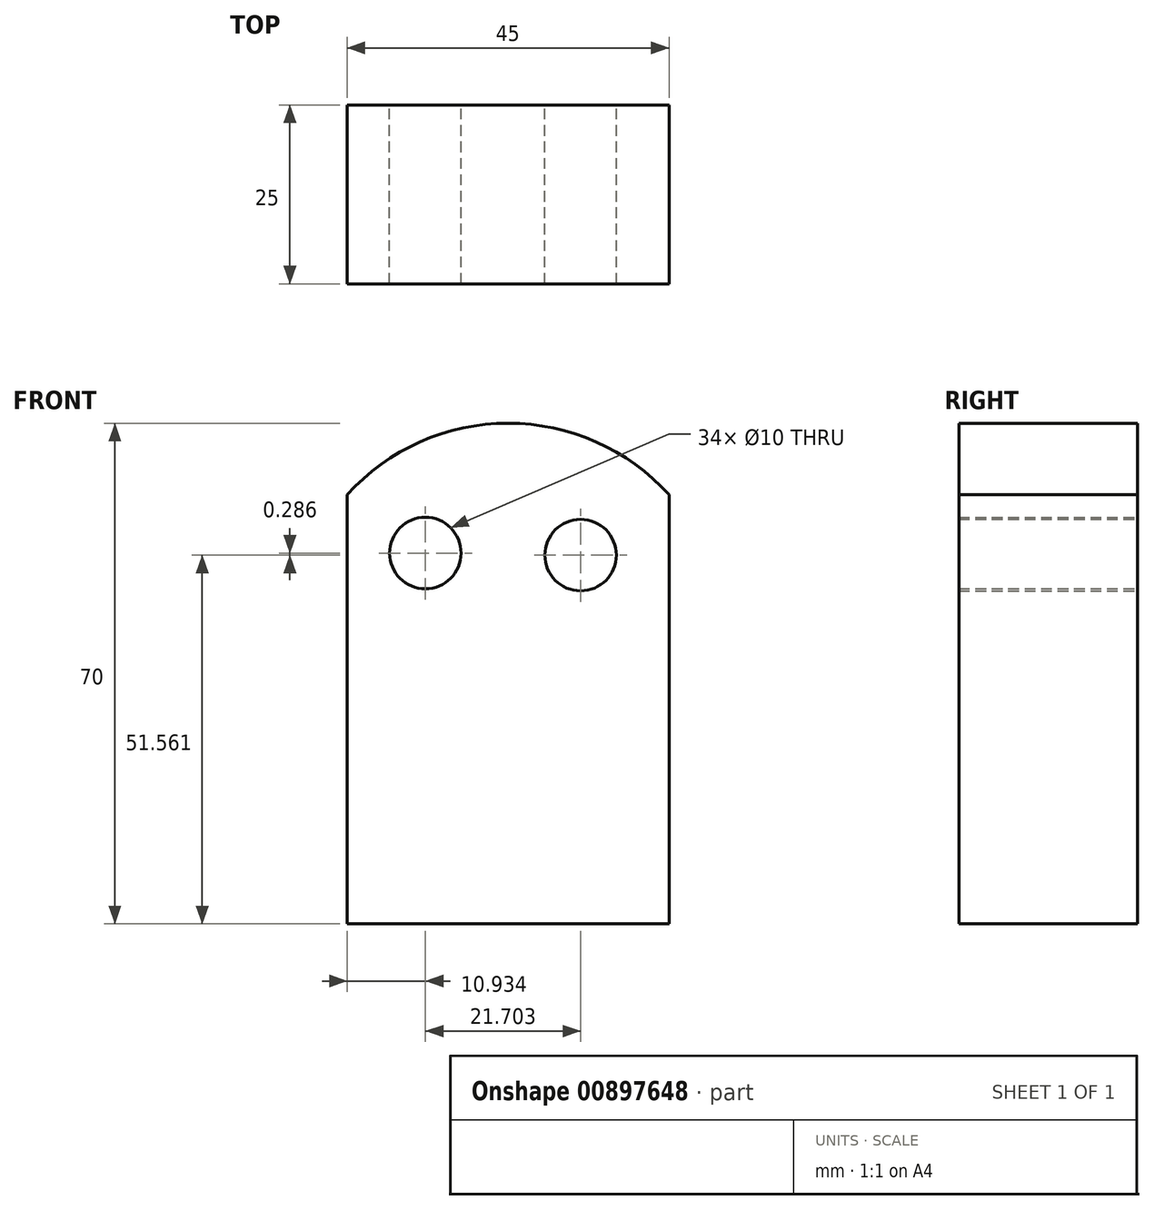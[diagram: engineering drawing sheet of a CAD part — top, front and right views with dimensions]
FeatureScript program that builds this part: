
annotation { "Feature Type Name" : "Feature", "Feature Type Description" : "" }
export const myFeature = defineFeature(function(context is Context, id is Id, definition is map)
    precondition{}
    {
        {
            var Q0;
            Q0=qCreatedBy(makeId("Front.planeOp"),FACE);
            var sketch = newSketch(context, id + "F0", { "sketchPlane" : qUnion([Q0])});
            skLineSegment(sketch, "E0.bottom", {"start": v(-22.5, 30) * mm, "end": v(22.5, 30) * mm});
            skLineSegment(sketch, "E0.top", {"start": v(-22.5, -30) * mm, "end": v(22.5, -30) * mm});
            skLineSegment(sketch, "E0.left", {"start": v(-22.5, 30) * mm, "end": v(-22.5, -30) * mm});
            skLineSegment(sketch, "E0.right", {"start": v(22.5, 30) * mm, "end": v(22.5, -30) * mm});
            skPoint(sketch, "E0.middle", {"position": v(0, 0) * mm});
            skArc(sketch, "E1", {"start": v(22.5, 30) * mm, "mid": v(0, 40) * mm, "end": v(-22.5, 30) * mm});
            skCircle(sketch, "E2", {"center": v(-11.57, 21.85) * mm, "radius": 5 * mm});
            skCircle(sketch, "E3", {"center": v(10.14, 21.56) * mm, "radius": 5 * mm});
            skSolve(sketch);
        }
        {
            var Q0;
            Q0=makeQuery(id+"F0.imprint","IMPRINT",FACE,{"disambiguationData":[TD([[makeQuery(id+"F0.imprint","IMPRINT",EDGE,{"derivedFrom":sQuery(id+"F0.wireOp",EDGE,"E0.bottom")}),1.0]])]});
            var Q1;
            Q1=makeQuery(id+"F0.imprint","IMPRINT",FACE,{"disambiguationData":[TD([[makeQuery(id+"F0.imprint","IMPRINT",EDGE,{"derivedFrom":sQuery(id+"F0.wireOp",EDGE,"E0.bottom")}),-1.0]])]});
            extrude(context, id + "F1", {"entities" : qUnion([Q0, Q1]), "depth" : 25 * mm, "offsetDistance" : 25.4 * mm});
        }
    });
